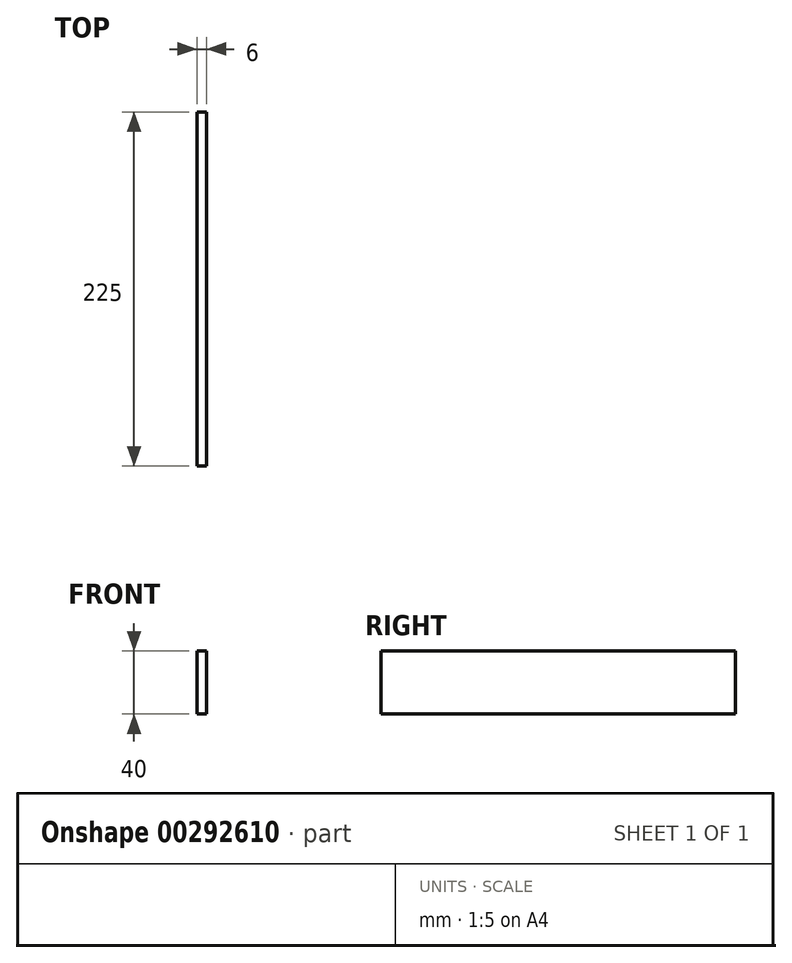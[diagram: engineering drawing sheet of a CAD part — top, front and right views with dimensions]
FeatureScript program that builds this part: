
annotation { "Feature Type Name" : "Feature", "Feature Type Description" : "" }
export const myFeature = defineFeature(function(context is Context, id is Id, definition is map)
    precondition{}
    {
        {
            var Q0;
            Q0=qCreatedBy(makeId("Front.planeOp"),FACE);
            var sketch = newSketch(context, id + "F0", { "sketchPlane" : qUnion([Q0])});
            skLineSegment(sketch, "E0", {"start": v(-7.05, 28.85) * mm, "end": v(-7.05, -11.15) * mm});
            skLineSegment(sketch, "E1", {"start": v(-7.05, -11.15) * mm, "end": v(-1.05, -11.15) * mm});
            skLineSegment(sketch, "E2", {"start": v(-7.05, 28.85) * mm, "end": v(-1.05, 28.85) * mm});
            skLineSegment(sketch, "E3", {"start": v(-1.05, 28.85) * mm, "end": v(-1.05, -11.15) * mm});
            skSolve(sketch);
        }
        {
            var Q0;
            Q0=makeQuery(id+"F0.imprint","IMPRINT",FACE,{"disambiguationData":[TD([[makeQuery(id+"F0.imprint","IMPRINT",EDGE,{"derivedFrom":sQuery(id+"F0.wireOp",EDGE,"E0")}),1.0]])]});
            extrude(context, id + "F1", {"entities" : qUnion([Q0]), "depth" : 225 * mm});
        }
    });
